# Revit family: LUXI_DOWNLIGHT_CC
name_source: partatom
category: Apparecchi per illuminazione
revit_build: Autodesk Revit 2016 (Build: 20161004_0715(x64)
units: mm (PartAtom-declared; Revit-internal decimal feet)

## family parameters
Condiviso = No
Host = Superficie
Numero OmniClass = 23.80.70.00
Punto di calcolo locali = Sì
Quota connettore circolare = Usa diametro
Sorgente d'illuminazione = Sì
Taglio con vuoti quando caricato = No
Tipo di parte = Normale
Titolo OmniClass = Lighting

## types (3) — shared parameters
Alimentatore = Incluso, non dimmerabile
Alimentazione = 220-240V AC / 50-60 Hz
Angolo inclinazione = -90.00°
Certificazioni = CE / RohS
Classe di efficienza energetica = A+
Classe di protezione = II
Classe di rischio fotobiologico = Esente (RG0)
Colore = Bianco (cornice)
Descrizione = LED Downlight
Fattore di correzione di potenza = ≥0,95 (typ.)
Filtro dei colori = 16777215
Garanzia = 5 anni
Grado di protezione = IP 20
IFCExportAs = IfcLightFixtureType
Masterformat 2016 Codice = 26.50.00
Masterformat 2016 Descrizione = Lighting
Materiale 1 = Policarbonato_Bianco
Materiale 2 = Tecnopolimero Opalino Diffondente
Materiale 3 = Alluminio_Grigio
Modello = Serie CC | Downlight
Ottiche = Riflettore metallizzato UGR≤19
Produttore = Luxi Illuminazione S.r.l.
Prospetto di default = 2000 mm  [stored 6.56168 ft]
Protezione agli urti = IK06 (1 Joule)
Regolazione del flusso luminoso = 1-10V / DALI / PUSH DIM (opzionali)
Rendi la forma visibile nel rendering = No
Revisione = 3
Sistema di illuminazione = luce indiretta (edge light)
Sorgente = LED SMD
Step MacAdam (SDCM) = <3
Temperatura di esercizio = 0°C / +40°C
Tipologie di installazione = Incasso
URL = https://www.luxi.lighting
Uniclass 2015 Codice = EF_70_80
Uniclass 2015 Descrizione = Lighting
Variazione temperatura colore lampada con luminosità attenuata = <Nessuno>
Vita utile = L70B20 50.000ore

## per-type parameters (varying)
| type | Carico apparente | Diametro | Dimensioni | Emetti da diametro cerchio | File diagramma fotometrico | H | Incasso | Indice di resa cromatica | OFF1 | OFF2 | OFF3 | Peso | Potenza |
| DLCC012120WX840 | 12 VA | 140 mm  [stored 0.459318 ft] | Ø140x68 incasso Ø120 | 105 mm | DLCC012120WX840 Luxi Serie CC 12W 4000K UGR19.IES | 68 mm | 120 mm  [stored 0.393701 ft] | ≥80 (typ.) | 41 mm | 45 mm  [stored 0.147638 ft] | 54 mm  [stored 0.177165 ft] | 0.32 kg | 12 W |
| DLCC022150WX940 | 22 VA | 180 mm  [stored 0.590551 ft] | Ø180x90 incasso Ø150 | 145 mm | DLCC022150WX840 Luxi Serie CC 22W 4000K UGR19.IES | 90 mm  [stored 0.295276 ft] | 150 mm | ≥90 (typ.) | 63 mm | 60 mm | 69 mm  [stored 0.226378 ft] | 0.52 kg | 22 W |
| DLCC032200WX840 | 32 VA | 230 mm  [stored 0.754593 ft] | Ø230x120 incasso Ø200 | 195 mm | DLCC032200WX840 Luxi Serie CC 32W 4000K UGR19.IES | 120 mm  [stored 0.393701 ft] | 200 mm  [stored 0.656168 ft] | ≥80 (typ.) | 93 mm | 85 mm  [stored 0.278871 ft] | 94 mm  [stored 0.308399 ft] | 0.92 kg | 32 W |

note: column(s) folded — value = type name in every type: Articolo

note: [stored X ft] marks values corroborated as IEEE doubles in the binary element streams (Revit-internal decimal feet)
